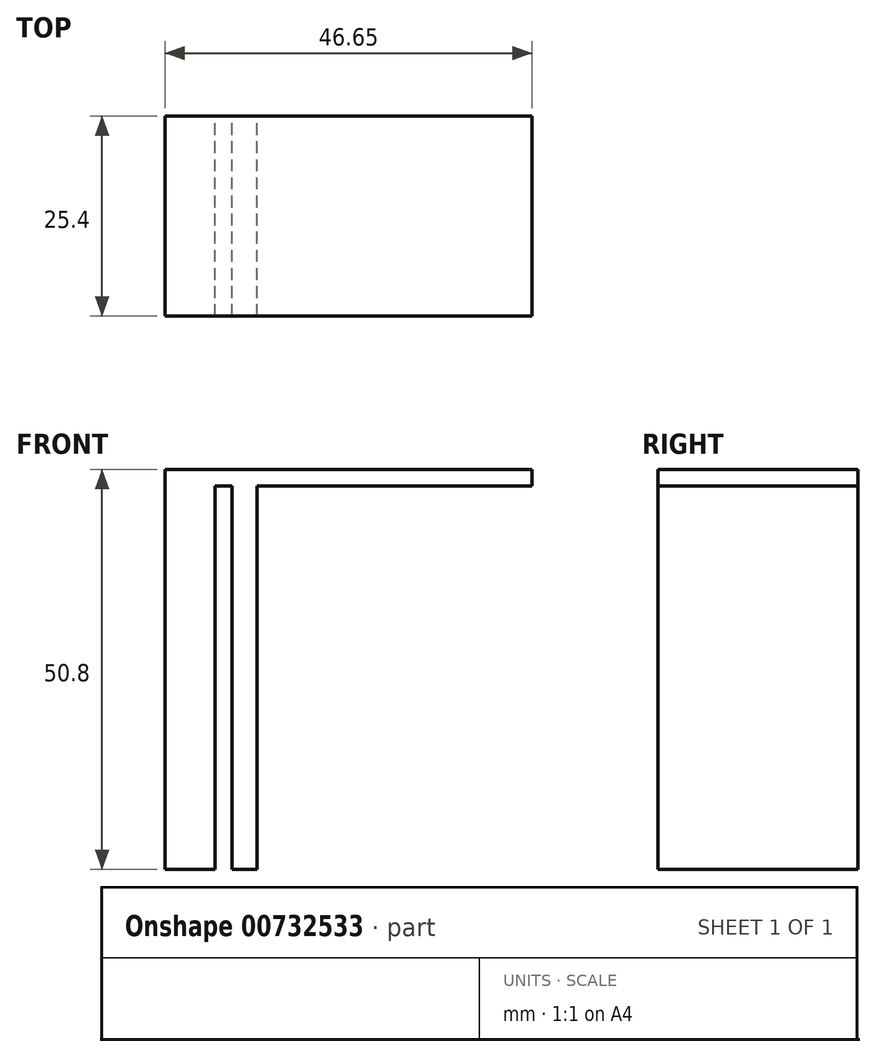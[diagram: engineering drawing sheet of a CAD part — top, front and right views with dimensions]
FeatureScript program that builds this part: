
annotation { "Feature Type Name" : "Feature", "Feature Type Description" : "" }
export const myFeature = defineFeature(function(context is Context, id is Id, definition is map)
    precondition{}
    {
        {
            var Q0;
            Q0=qCreatedBy(makeId("Front.planeOp"),FACE);
            var sketch = newSketch(context, id + "F0", { "sketchPlane" : qUnion([Q0])});
            skLineSegment(sketch, "E0", {"start": v(-34, 12.81) * mm, "end": v(-34, 63.61) * mm});
            skLineSegment(sketch, "E1", {"start": v(-34, 63.61) * mm, "end": v(-31.8, 63.61) * mm});
            skLineSegment(sketch, "E2", {"start": v(-31.8, 63.61) * mm, "end": v(-31.8, 12.81) * mm});
            skLineSegment(sketch, "E3", {"start": v(-31.8, 63.61) * mm, "end": v(6.3, 63.61) * mm});
            skLineSegment(sketch, "E4", {"start": v(-31.8, 61.51) * mm, "end": v(6.3, 61.51) * mm});
            skLineSegment(sketch, "E5", {"start": v(6.3, 61.51) * mm, "end": v(6.3, 63.61) * mm});
            skLineSegment(sketch, "E6", {"start": v(-34, 12.81) * mm, "end": v(-40.35, 12.81) * mm});
            skLineSegment(sketch, "E7", {"start": v(-40.35, 12.81) * mm, "end": v(-40.35, 63.61) * mm});
            skLineSegment(sketch, "E8", {"start": v(-40.35, 63.61) * mm, "end": v(-34, 63.61) * mm});
            skLineSegment(sketch, "E9", {"start": v(-31.8, 12.81) * mm, "end": v(-28.63, 12.81) * mm});
            skLineSegment(sketch, "E10", {"start": v(-28.63, 12.81) * mm, "end": v(-28.63, 61.51) * mm});
            skLineSegment(sketch, "E11", {"start": v(-31.8, 61.51) * mm, "end": v(-34, 61.51) * mm});
            skSolve(sketch);
        }
        {
            var Q0;
            {var subQ0=sQuery(id+"F0.wireOp",EDGE,"E6");Q0=makeQuery(id+"F0.imprint","IMPRINT",FACE,{"disambiguationData":[TD([[makeQuery(id+"F0.imprint","IMPRINT",EDGE,{"derivedFrom":subQ0}),-1.0]])]});}
            var Q1;
            {var subQ0=sQuery(id+"F0.wireOp",EDGE,"E9");Q1=makeQuery(id+"F0.imprint","IMPRINT",FACE,{"disambiguationData":[TD([[makeQuery(id+"F0.imprint","IMPRINT",EDGE,{"derivedFrom":subQ0}),1.0]])]});}
            var Q2;
            {var subQ0=sQuery(id+"F0.wireOp",EDGE,"E1");Q2=makeQuery(id+"F0.imprint","IMPRINT",FACE,{"disambiguationData":[TD([[makeQuery(id+"F0.imprint","IMPRINT",EDGE,{"derivedFrom":subQ0}),-1.0]])]});}
            var Q3;
            {var subQ5=sQuery(id+"F0.wireOp",EDGE,"E3");Q3=makeQuery(id+"F0.imprint","IMPRINT",FACE,{"disambiguationData":[TD([[makeQuery(id+"F0.imprint","IMPRINT",EDGE,{"derivedFrom":subQ5}),-1.0]])]});}
            extrude(context, id + "F1", {"entities" : qUnion([Q0, Q1, Q2, Q3]), "depth" : 25.4 * mm, "offsetDistance" : 25.4 * mm});
        }
    });
